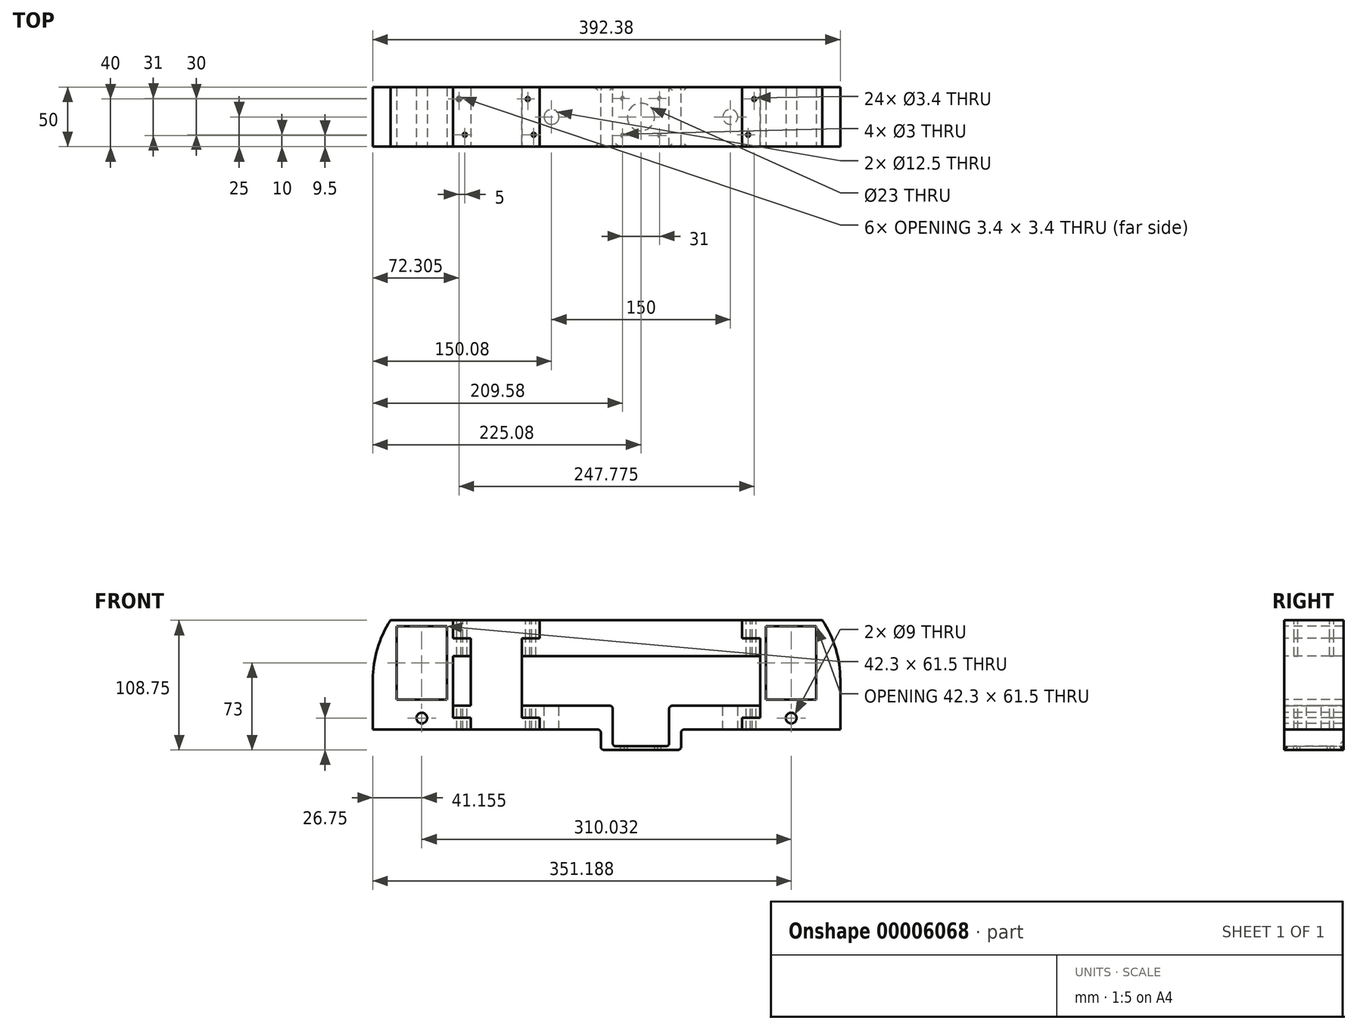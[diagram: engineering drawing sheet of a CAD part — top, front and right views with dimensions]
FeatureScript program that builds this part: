
annotation { "Feature Type Name" : "Feature", "Feature Type Description" : "" }
export const myFeature = defineFeature(function(context is Context, id is Id, definition is map)
    precondition{}
    {
        {
            var Q0;
            Q0=qCreatedBy(makeId("Front.planeOp"),FACE);
            var sketch = newSketch(context, id + "F0", { "sketchPlane" : qUnion([Q0])});
            skLineSegment(sketch, "E0", {"start": v(66.35, 0) * mm, "end": v(66.35, -17) * mm});
            skLineSegment(sketch, "E1", {"start": v(66.35, -17) * mm, "end": v(133.65, -17) * mm});
            skLineSegment(sketch, "E2", {"start": v(133.65, -17) * mm, "end": v(133.65, 0) * mm});
            skLineSegment(sketch, "E3", {"start": v(200, 20) * mm, "end": v(123.65, 20) * mm});
            skLineSegment(sketch, "E4", {"start": v(123.65, 20) * mm, "end": v(123.65, -14) * mm});
            skLineSegment(sketch, "E5", {"start": v(123.65, -14) * mm, "end": v(76.35, -14) * mm});
            skLineSegment(sketch, "E6", {"start": v(76.35, -14) * mm, "end": v(76.35, 20) * mm});
            skLineSegment(sketch, "E7", {"start": v(76.35, 20) * mm, "end": v(0, 20) * mm});
            skLineSegment(sketch, "E8", {"start": v(133.65, 0) * mm, "end": v(185, 0) * mm});
            skLineSegment(sketch, "E9", {"start": v(185, 0) * mm, "end": v(185, 10) * mm});
            skLineSegment(sketch, "E10", {"start": v(185, 10) * mm, "end": v(200, 10) * mm});
            skLineSegment(sketch, "E11", {"start": v(200, 10) * mm, "end": v(200, 20) * mm});
            skLineSegment(sketch, "E12", {"start": v(66.35, 0) * mm, "end": v(15, 0) * mm});
            skLineSegment(sketch, "E13", {"start": v(15, 0) * mm, "end": v(15, 10) * mm});
            skLineSegment(sketch, "E14", {"start": v(15, 10) * mm, "end": v(0, 10) * mm});
            skLineSegment(sketch, "E15", {"start": v(0, 10) * mm, "end": v(0, 20) * mm});
            skSolve(sketch);
        }
        {
            var Q0;
            Q0 = qSketchRegion(id + "F0", true);
            extrude(context, id + "F1", {"entities" : qUnion([Q0]), "depth" : 50 * mm});
        }
        {
            var Q0;
            Q0=makeQuery(id+"F1.opExtrude","SWEPT_EDGE",EDGE,{"disambiguationData":[OSD([sQuery(id+"F0.wireOp",EDGE,"E4"),sQuery(id+"F0.wireOp",EDGE,"E5")])]});
            var Q1;
            Q1=makeQuery(id+"F1.opExtrude","SWEPT_EDGE",EDGE,{"disambiguationData":[OSD([sQuery(id+"F0.wireOp",EDGE,"E5"),sQuery(id+"F0.wireOp",EDGE,"E6")])]});
            var Q2;
            Q2=makeQuery(id+"F1.opExtrude","SWEPT_EDGE",EDGE,{"disambiguationData":[OSD([sQuery(id+"F0.wireOp",EDGE,"E1"),sQuery(id+"F0.wireOp",EDGE,"E2")])]});
            var Q3;
            Q3=makeQuery(id+"F1.opExtrude","SWEPT_EDGE",EDGE,{"disambiguationData":[OSD([sQuery(id+"F0.wireOp",EDGE,"E0"),sQuery(id+"F0.wireOp",EDGE,"E1")])]});
            var Q4;
            Q4=makeQuery(id+"F1.opExtrude","SWEPT_EDGE",EDGE,{"disambiguationData":[OSD([sQuery(id+"F0.wireOp",EDGE,"25d413c4-04d7-459c-bcf7-bf226ccfaa6d"),sQuery(id+"F0.wireOp",EDGE,"E0")])]});
            var Q5;
            Q5=makeQuery(id+"F1.opExtrude","SWEPT_EDGE",EDGE,{"disambiguationData":[OSD([sQuery(id+"F0.wireOp",EDGE,"E2"),sQuery(id+"F0.wireOp",EDGE,"8273c938-ca82-47b6-a2fe-12fa87529be1")])]});
            var Q6;
            Q6=makeQuery(id+"F1.opExtrude","SWEPT_EDGE",EDGE,{"disambiguationData":[OSD([sQuery(id+"F0.wireOp",EDGE,"E3"),sQuery(id+"F0.wireOp",EDGE,"E4")])]});
            var Q7;
            Q7=makeQuery(id+"F1.opExtrude","SWEPT_EDGE",EDGE,{"disambiguationData":[OSD([sQuery(id+"F0.wireOp",EDGE,"E6"),sQuery(id+"F0.wireOp",EDGE,"E7")])]});
            var Q8;
            Q8=makeQuery(id+"F1.opExtrude","CAP_EDGE",EDGE,{"disambiguationData":[OSD([sQuery(id+"F0.wireOp",EDGE,"E7")])],"isStart":false});
            var Q9;
            Q9=makeQuery(id+"F1.opExtrude","CAP_EDGE",EDGE,{"disambiguationData":[OSD([sQuery(id+"F0.wireOp",EDGE,"E3")])],"isStart":false});
            var Q10;
            Q10=makeQuery(id+"F1.opExtrude","CAP_EDGE",EDGE,{"disambiguationData":[OSD([sQuery(id+"F0.wireOp",EDGE,"E3")])],"isStart":true});
            var Q11;
            Q11=makeQuery(id+"F1.opExtrude","CAP_EDGE",EDGE,{"disambiguationData":[OSD([sQuery(id+"F0.wireOp",EDGE,"E7")])],"isStart":true});
            var Q12;
            Q12=makeQuery(id+"F1.opExtrude","CAP_EDGE",EDGE,{"disambiguationData":[OSD([sQuery(id+"F0.wireOp",EDGE,"E6")])],"isStart":false});
            var Q13;
            Q13=makeQuery(id+"F1.opExtrude","CAP_EDGE",EDGE,{"disambiguationData":[OSD([sQuery(id+"F0.wireOp",EDGE,"E2")])],"isStart":false});
            var Q14;
            Q14=makeQuery(id+"F1.opExtrude","CAP_EDGE",EDGE,{"disambiguationData":[OSD([sQuery(id+"F0.wireOp",EDGE,"E0")])],"isStart":false});
            var Q15;
            Q15=makeQuery(id+"F1.opExtrude","CAP_EDGE",EDGE,{"disambiguationData":[OSD([sQuery(id+"F0.wireOp",EDGE,"E5")])],"isStart":true});
            var Q16;
            Q16=makeQuery(id+"F1.opExtrude","CAP_EDGE",EDGE,{"disambiguationData":[OSD([sQuery(id+"F0.wireOp",EDGE,"E2")])],"isStart":true});
            var Q17;
            Q17=makeQuery(id+"F1.opExtrude","CAP_EDGE",EDGE,{"disambiguationData":[OSD([sQuery(id+"F0.wireOp",EDGE,"E0")])],"isStart":true});
            fillet(context, id + "F2", {"entities" : qUnion([Q0, Q1, Q2, Q3, Q4, Q5, Q6, Q7, Q8, Q9, Q10, Q11, Q12, Q13, Q14, Q15, Q16, Q17]), "radius" : 2.5 * mm, "tangentPropagation" : true, "allowEdgeOverflow" : false});
        }
        {
            var Q0;
            Q0=makeQuery(id+"F1.opExtrude","SWEPT_FACE",FACE,{"disambiguationData":[OSD([sQuery(id+"F0.wireOp",EDGE,"E5")])]});
            var sketch = newSketch(context, id + "F3", { "sketchPlane" : qUnion([Q0])});
            skLineSegment(sketch, "E16.bottom", {"start": v(78.85, -3.85) * mm, "end": v(121.15, -3.85) * mm, "construction": true});
            skLineSegment(sketch, "E16.top", {"start": v(78.85, -46.15) * mm, "end": v(121.15, -46.15) * mm, "construction": true});
            skLineSegment(sketch, "E16.left", {"start": v(78.85, -3.85) * mm, "end": v(78.85, -46.15) * mm, "construction": true});
            skLineSegment(sketch, "E16.right", {"start": v(121.15, -3.85) * mm, "end": v(121.15, -46.15) * mm, "construction": true});
            skLineSegment(sketch, "E17", {"start": v(100, -3.85) * mm, "end": v(100, -2.5) * mm, "construction": true});
            skLineSegment(sketch, "E18", {"start": v(100, -46.15) * mm, "end": v(100, -47.5) * mm, "construction": true});
            skLineSegment(sketch, "E19", {"start": v(78.85, -3.85) * mm, "end": v(121.15, -46.15) * mm, "construction": true});
            skLineSegment(sketch, "E20", {"start": v(78.85, -46.15) * mm, "end": v(121.15, -3.85) * mm, "construction": true});
            skLineSegment(sketch, "E21", {"start": v(84.5, -9.5) * mm, "end": v(115.5, -9.5) * mm, "construction": true});
            skLineSegment(sketch, "E22", {"start": v(115.5, -9.5) * mm, "end": v(115.5, -40.5) * mm, "construction": true});
            skLineSegment(sketch, "E23", {"start": v(115.5, -40.5) * mm, "end": v(84.5, -40.5) * mm, "construction": true});
            skLineSegment(sketch, "E24", {"start": v(84.5, -40.5) * mm, "end": v(84.5, -9.5) * mm, "construction": true});
            skCircle(sketch, "E25", {"center": v(84.5, -9.5) * mm, "radius": 1.5 * mm});
            skCircle(sketch, "E26", {"center": v(115.5, -9.5) * mm, "radius": 1.5 * mm});
            skCircle(sketch, "E27", {"center": v(115.5, -40.5) * mm, "radius": 1.5 * mm});
            skCircle(sketch, "E28", {"center": v(84.5, -40.5) * mm, "radius": 1.5 * mm});
            skCircle(sketch, "E29", {"center": v(100, -25) * mm, "radius": 11.5 * mm});
            skSolve(sketch);
        }
        {
            var Q0;
            Q0 = qSketchRegion(id + "F3", true);
            extrude(context, id + "F4", {"entities" : qUnion([Q0]), "operationType" : NewBodyOperationType.REMOVE, "oppositeDirection" : true, "depth" : 25 * mm});
        }
        {
            var Q0;
            Q0=makeQuery(id+"F1.opExtrude","CAP_FACE",FACE,{"disambiguationData":[OSD([sQuery(id+"F0.wireOp",EDGE,"7cd8d7bc-7dec-443a-83b3-ba99ea593d57"),sQuery(id+"F0.wireOp",EDGE,"59747b56-2e24-4794-8826-f2c9fe0a8e2f"),sQuery(id+"F0.wireOp",EDGE,"60e4274c-6528-4dbb-8c65-7a1c295b8255"),sQuery(id+"F0.wireOp",EDGE,"69b43952-8336-45bf-9730-06b1f1448a6f"),sQuery(id+"F0.wireOp",EDGE,"a2af3474-0233-43bb-83cb-60ed80dac262"),sQuery(id+"F0.wireOp",EDGE,"25d413c4-04d7-459c-bcf7-bf226ccfaa6d"),sQuery(id+"F0.wireOp",EDGE,"E0"),sQuery(id+"F0.wireOp",EDGE,"E1"),sQuery(id+"F0.wireOp",EDGE,"E2"),sQuery(id+"F0.wireOp",EDGE,"8273c938-ca82-47b6-a2fe-12fa87529be1"),sQuery(id+"F0.wireOp",EDGE,"4707e04e-d9cc-4bb7-a771-f1b94968c0b5"),sQuery(id+"F0.wireOp",EDGE,"26d6e5ed-fd12-44b5-9e14-1d22e9212bdb"),sQuery(id+"F0.wireOp",EDGE,"6fa0b8f3-1a7a-4232-9b85-c42c3082a16d"),sQuery(id+"F0.wireOp",EDGE,"91bd62d1-c68c-4093-848f-cc9b293d17f5"),sQuery(id+"F0.wireOp",EDGE,"8c203d04-b222-4ccc-a70f-71613ceaa2ef"),sQuery(id+"F0.wireOp",EDGE,"E3"),sQuery(id+"F0.wireOp",EDGE,"E4"),sQuery(id+"F0.wireOp",EDGE,"E5"),sQuery(id+"F0.wireOp",EDGE,"E6"),sQuery(id+"F0.wireOp",EDGE,"E7")])],"isStart":false});
            var sketch = newSketch(context, id + "F5", { "sketchPlane" : qUnion([Q0])});
            skLineSegment(sketch, "E30", {"start": v(247.26, 86.75) * mm, "end": v(204.96, 86.75) * mm});
            skLineSegment(sketch, "E31", {"start": v(226.1, 86.75) * mm, "end": v(226.1, -5.25) * mm, "construction": true});
            skCircle(sketch, "E32", {"center": v(226.1, 9.75) * mm, "radius": 4.5 * mm});
            skLineSegment(sketch, "E33", {"start": v(226.1, 9.75) * mm, "end": v(226.1, 25.25) * mm, "construction": true});
            skLineSegment(sketch, "E34", {"start": v(226.1, 25.25) * mm, "end": v(204.96, 25.25) * mm});
            skLineSegment(sketch, "E35", {"start": v(204.96, 25.25) * mm, "end": v(204.96, 86.75) * mm});
            skLineSegment(sketch, "E36.bottom", {"start": v(267.3, 91.75) * mm, "end": v(252.3, 91.75) * mm, "construction": true});
            skLineSegment(sketch, "E36.top", {"start": v(267.3, 41.75) * mm, "end": v(252.3, 41.75) * mm, "construction": true});
            skLineSegment(sketch, "E36.left", {"start": v(267.3, 91.75) * mm, "end": v(267.3, 41.75) * mm, "construction": true});
            skLineSegment(sketch, "E36.right", {"start": v(252.3, 91.75) * mm, "end": v(252.3, 41.75) * mm, "construction": true});
            skLineSegment(sketch, "E37", {"start": v(252.3, 91.75) * mm, "end": v(200, 91.75) * mm});
            skArc(sketch, "E38", {"start": v(267.3, 41.75) * mm, "mid": v(263.47, 67.85) * mm, "end": v(252.3, 91.75) * mm});
            skLineSegment(sketch, "E39", {"start": v(226.1, 25.25) * mm, "end": v(247.26, 25.25) * mm});
            skLineSegment(sketch, "E40", {"start": v(247.26, 86.75) * mm, "end": v(247.26, 25.25) * mm});
            skLineSegment(sketch, "E41", {"start": v(185, 10) * mm, "end": v(200, 10) * mm});
            skLineSegment(sketch, "E42", {"start": v(200, 91.75) * mm, "end": v(185, 91.75) * mm});
            skLineSegment(sketch, "E43", {"start": v(185, 91.75) * mm, "end": v(185, 76.75) * mm});
            skLineSegment(sketch, "E44", {"start": v(185, 76.75) * mm, "end": v(200, 76.75) * mm});
            skLineSegment(sketch, "E45", {"start": v(200, 10) * mm, "end": v(200, 76.75) * mm});
            skLineSegment(sketch, "E46", {"start": v(185, 10) * mm, "end": v(185, 0) * mm});
            skLineSegment(sketch, "E47", {"start": v(185, 0) * mm, "end": v(267.3, 0) * mm});
            skLineSegment(sketch, "E48", {"start": v(267.3, 41.75) * mm, "end": v(267.3, 0) * mm});
            skSolve(sketch);
        }
        {
            var Q0;
            Q0=makeQuery(id+"F1.opExtrude","SWEPT_FACE",FACE,{"disambiguationData":[OSD([sQuery(id+"F0.wireOp",EDGE,"E7")])]});
            var sketch = newSketch(context, id + "F6", { "sketchPlane" : qUnion([Q0])});
            skCircle(sketch, "E49", {"center": v(25, -25) * mm, "radius": 6.25 * mm});
            skCircle(sketch, "E50", {"center": v(175, -25) * mm, "radius": 6.25 * mm});
            skCircle(sketch, "E51", {"center": v(5, -10) * mm, "radius": 1.7 * mm});
            skCircle(sketch, "E52", {"center": v(10, -40) * mm, "radius": 1.7 * mm});
            skCircle(sketch, "E53", {"center": v(190, -40) * mm, "radius": 1.7 * mm});
            skCircle(sketch, "E54", {"center": v(195, -10) * mm, "radius": 1.7 * mm});
            skSolve(sketch);
        }
        {
            var Q0;
            Q0 = qSketchRegion(id + "F6", true);
            extrude(context, id + "F7", {"entities" : qUnion([Q0]), "operationType" : NewBodyOperationType.REMOVE, "endBound" : BoundingType.THROUGH_ALL, "depth" : 25 * mm});
        }
        {
            var Q0;
            Q0 = qSketchRegion(id + "F5", true);
            extrude(context, id + "F8", {"entities" : qUnion([Q0]), "oppositeDirection" : true, "depth" : 50 * mm});
        }
        {
            var Q0;
            Q0=makeQuery(id+"F8.opExtrude","CAP_FACE",FACE,{"disambiguationData":[OSD([sQuery(id+"F5.wireOp",EDGE,"E30"),sQuery(id+"F5.wireOp",EDGE,"E32"),sQuery(id+"F5.wireOp",EDGE,"E34"),sQuery(id+"F5.wireOp",EDGE,"E35"),sQuery(id+"F5.wireOp",EDGE,"E37"),sQuery(id+"F5.wireOp",EDGE,"E38"),sQuery(id+"F5.wireOp",EDGE,"E39"),sQuery(id+"F5.wireOp",EDGE,"E40"),sQuery(id+"F5.wireOp",EDGE,"E41"),sQuery(id+"F5.wireOp",EDGE,"E42"),sQuery(id+"F5.wireOp",EDGE,"E43"),sQuery(id+"F5.wireOp",EDGE,"E44"),sQuery(id+"F5.wireOp",EDGE,"E45"),sQuery(id+"F5.wireOp",EDGE,"E46"),sQuery(id+"F5.wireOp",EDGE,"E47"),sQuery(id+"F5.wireOp",EDGE,"E48")])],"isStart":true});
            var sketch = newSketch(context, id + "F9", { "sketchPlane" : qUnion([Q0])});
            skLineSegment(sketch, "E55", {"start": v(200, 76.75) * mm, "end": v(200, 61.75) * mm});
            skLineSegment(sketch, "E56", {"start": v(200, 76.75) * mm, "end": v(185, 76.75) * mm});
            skLineSegment(sketch, "E57", {"start": v(185, 76.75) * mm, "end": v(185, 91.75) * mm});
            skLineSegment(sketch, "E58", {"start": v(185, 91.75) * mm, "end": v(15, 91.75) * mm});
            skLineSegment(sketch, "E59", {"start": v(15, 91.75) * mm, "end": v(15, 76.75) * mm});
            skLineSegment(sketch, "E60", {"start": v(15, 76.75) * mm, "end": v(0, 76.75) * mm});
            skLineSegment(sketch, "E61", {"start": v(0, 76.75) * mm, "end": v(0, 61.75) * mm});
            skLineSegment(sketch, "E62", {"start": v(0, 61.75) * mm, "end": v(200, 61.75) * mm});
            skSolve(sketch);
        }
        {
            var Q0;
            Q0 = qSketchRegion(id + "F9", true);
            extrude(context, id + "F10", {"entities" : qUnion([Q0]), "oppositeDirection" : true, "depth" : 50 * mm});
        }
        {
            var Q0;
            Q0=makeQuery(id+"F10.opExtrude","CAP_FACE",FACE,{"disambiguationData":[OSD([sQuery(id+"F9.wireOp",EDGE,"E55"),sQuery(id+"F9.wireOp",EDGE,"E56"),sQuery(id+"F9.wireOp",EDGE,"E57"),sQuery(id+"F9.wireOp",EDGE,"E58"),sQuery(id+"F9.wireOp",EDGE,"E59"),sQuery(id+"F9.wireOp",EDGE,"E60"),sQuery(id+"F9.wireOp",EDGE,"E61"),sQuery(id+"F9.wireOp",EDGE,"E62")])],"isStart":true});
            var sketch = newSketch(context, id + "F11", { "sketchPlane" : qUnion([Q0])});
            skLineSegment(sketch, "E63", {"start": v(15, 91.75) * mm, "end": v(15, 76.75) * mm});
            skLineSegment(sketch, "E64", {"start": v(15, 76.75) * mm, "end": v(0, 76.75) * mm});
            skLineSegment(sketch, "E65", {"start": v(0, 76.75) * mm, "end": v(0, 10) * mm});
            skLineSegment(sketch, "E66", {"start": v(0, 10) * mm, "end": v(15, 10) * mm});
            skLineSegment(sketch, "E67", {"start": v(15, 10) * mm, "end": v(15, 0) * mm});
            skLineSegment(sketch, "E68", {"start": v(15, 0) * mm, "end": v(-42.78, 0) * mm});
            skLineSegment(sketch, "E69", {"start": v(-42.78, 0) * mm, "end": v(-42.78, 10) * mm});
            skLineSegment(sketch, "E70", {"start": v(-42.78, 10) * mm, "end": v(-57.78, 10) * mm});
            skLineSegment(sketch, "E71", {"start": v(-57.78, 10) * mm, "end": v(-57.78, 20) * mm});
            skLineSegment(sketch, "E72", {"start": v(-57.78, 20) * mm, "end": v(-42.78, 20) * mm});
            skLineSegment(sketch, "E73", {"start": v(-42.78, 20) * mm, "end": v(-42.78, 76.75) * mm});
            skLineSegment(sketch, "E74", {"start": v(-42.78, 76.75) * mm, "end": v(-57.78, 76.75) * mm});
            skLineSegment(sketch, "E75", {"start": v(-57.78, 76.75) * mm, "end": v(-57.78, 91.75) * mm});
            skLineSegment(sketch, "E76", {"start": v(-57.78, 91.75) * mm, "end": v(15, 91.75) * mm});
            skSolve(sketch);
        }
        {
            var Q0;
            Q0 = qSketchRegion(id + "F11", true);
            extrude(context, id + "F12", {"entities" : qUnion([Q0]), "oppositeDirection" : true, "depth" : 50 * mm});
        }
        {
            var Q0;
            Q0=makeQuery(id+"F12.opExtrude","CAP_FACE",FACE,{"disambiguationData":[OSD([sQuery(id+"F11.wireOp",EDGE,"E63"),sQuery(id+"F11.wireOp",EDGE,"E64"),sQuery(id+"F11.wireOp",EDGE,"E65"),sQuery(id+"F11.wireOp",EDGE,"E66"),sQuery(id+"F11.wireOp",EDGE,"E67"),sQuery(id+"F11.wireOp",EDGE,"E68"),sQuery(id+"F11.wireOp",EDGE,"E69"),sQuery(id+"F11.wireOp",EDGE,"E70"),sQuery(id+"F11.wireOp",EDGE,"E71"),sQuery(id+"F11.wireOp",EDGE,"E72"),sQuery(id+"F11.wireOp",EDGE,"E73"),sQuery(id+"F11.wireOp",EDGE,"E74"),sQuery(id+"F11.wireOp",EDGE,"E75"),sQuery(id+"F11.wireOp",EDGE,"E76"),sQuery(id+"F11.wireOp",EDGE,"a7328c5a-23c9-4590-84e1-86b060998002"),sQuery(id+"F11.wireOp",EDGE,"49678679-c78d-463e-80d5-f9fdda81f58f"),sQuery(id+"F11.wireOp",EDGE,"c6644c5c-7cd0-4a62-a678-3d565e289008"),sQuery(id+"F11.wireOp",EDGE,"f0cade5a-4763-4761-80b8-ea56b3358b8d")])],"isStart":true});
            var sketch = newSketch(context, id + "F13", { "sketchPlane" : qUnion([Q0])});
            skLineSegment(sketch, "E77", {"start": v(-42.78, 76.75) * mm, "end": v(-57.78, 76.75) * mm});
            skLineSegment(sketch, "E78", {"start": v(-57.78, 76.75) * mm, "end": v(-57.78, 91.75) * mm});
            skLineSegment(sketch, "E79", {"start": v(-110.08, 91.75) * mm, "end": v(-125.08, 91.75) * mm, "construction": true});
            skLineSegment(sketch, "E80", {"start": v(-125.08, 91.75) * mm, "end": v(-125.08, 41.75) * mm, "construction": true});
            skLineSegment(sketch, "E81", {"start": v(-125.08, 41.75) * mm, "end": v(-110.08, 41.75) * mm, "construction": true});
            skLineSegment(sketch, "E82", {"start": v(-110.08, 41.75) * mm, "end": v(-110.08, 91.75) * mm, "construction": true});
            skArc(sketch, "E83", {"start": v(-110.08, 91.75) * mm, "mid": v(-121.24, 67.85) * mm, "end": v(-125.08, 41.75) * mm});
            skLineSegment(sketch, "E84", {"start": v(-125.08, 41.75) * mm, "end": v(-125.08, 0) * mm});
            skLineSegment(sketch, "E85", {"start": v(-125.08, 0) * mm, "end": v(-42.78, 0) * mm});
            skLineSegment(sketch, "E86", {"start": v(-42.78, 0) * mm, "end": v(-42.78, 10) * mm});
            skLineSegment(sketch, "E87", {"start": v(-42.78, 10) * mm, "end": v(-57.78, 10) * mm});
            skLineSegment(sketch, "E88", {"start": v(-57.78, 10) * mm, "end": v(-57.78, 20) * mm});
            skLineSegment(sketch, "E89", {"start": v(-42.78, 76.75) * mm, "end": v(-42.78, 61.75) * mm});
            skLineSegment(sketch, "E90", {"start": v(-42.78, 61.75) * mm, "end": v(-57.78, 61.75) * mm});
            skLineSegment(sketch, "E91", {"start": v(-57.78, 61.75) * mm, "end": v(-57.78, 20) * mm});
            skLineSegment(sketch, "E92", {"start": v(-110.08, 91.75) * mm, "end": v(-57.78, 91.75) * mm});
            skLineSegment(sketch, "E93", {"start": v(-62.78, 91.75) * mm, "end": v(-62.78, 86.75) * mm, "construction": true});
            skLineSegment(sketch, "E94", {"start": v(-62.78, 86.75) * mm, "end": v(-57.78, 86.75) * mm, "construction": true});
            skLineSegment(sketch, "E95", {"start": v(-62.78, 86.75) * mm, "end": v(-105.08, 86.75) * mm});
            skLineSegment(sketch, "E96", {"start": v(-105.08, 86.75) * mm, "end": v(-105.08, 25.25) * mm});
            skLineSegment(sketch, "E97", {"start": v(-105.08, 25.25) * mm, "end": v(-62.78, 25.25) * mm});
            skLineSegment(sketch, "E98", {"start": v(-62.78, 25.25) * mm, "end": v(-62.78, 86.75) * mm});
            skLineSegment(sketch, "E99", {"start": v(-83.93, 86.75) * mm, "end": v(-83.93, 0) * mm, "construction": true});
            skPoint(sketch, "E100", {"position": v(-83.93, 25.25) * mm});
            skCircle(sketch, "E101", {"center": v(-83.93, 9.75) * mm, "radius": 4.5 * mm});
            skSolve(sketch);
        }
        {
            var Q0;
            Q0 = qSketchRegion(id + "F13", true);
            extrude(context, id + "F14", {"entities" : qUnion([Q0]), "oppositeDirection" : true, "depth" : 50 * mm});
        }
        {
            var Q0;
            Q0 = qSketchRegion(id + "F6", true);
            extrude(context, id + "F15", {"entities" : qUnion([Q0]), "operationType" : NewBodyOperationType.REMOVE, "endBound" : BoundingType.THROUGH_ALL, "oppositeDirection" : true, "depth" : 25 * mm});
        }
        {
            var Q0;
            Q0=makeQuery(id+"F12.opExtrude","SWEPT_FACE",FACE,{"disambiguationData":[OSD([sQuery(id+"F11.wireOp",EDGE,"E76")])]});
            var sketch = newSketch(context, id + "F16", { "sketchPlane" : qUnion([Q0])});
            skLineSegment(sketch, "E102.bottom", {"start": v(-57.78, -50) * mm, "end": v(-42.78, -50) * mm, "construction": true});
            skLineSegment(sketch, "E102.top", {"start": v(-57.78, 0) * mm, "end": v(-42.78, 0) * mm, "construction": true});
            skLineSegment(sketch, "E102.left", {"start": v(-57.78, -50) * mm, "end": v(-57.78, 0) * mm, "construction": true});
            skLineSegment(sketch, "E102.right", {"start": v(-42.78, -50) * mm, "end": v(-42.78, 0) * mm, "construction": true});
            skLineSegment(sketch, "E103", {"start": v(-47.78, 0) * mm, "end": v(-47.78, -50) * mm, "construction": true});
            skLineSegment(sketch, "E104", {"start": v(-52.78, 0) * mm, "end": v(-52.78, -50) * mm, "construction": true});
            skLineSegment(sketch, "E105", {"start": v(-57.78, -40) * mm, "end": v(-42.78, -40) * mm, "construction": true});
            skLineSegment(sketch, "E106", {"start": v(-57.78, -10) * mm, "end": v(-42.78, -10) * mm, "construction": true});
            skCircle(sketch, "E107", {"center": v(-47.78, -40) * mm, "radius": 1.7 * mm});
            skCircle(sketch, "E108", {"center": v(-52.78, -10) * mm, "radius": 1.7 * mm});
            skSolve(sketch);
        }
        {
            var Q0;
            Q0 = qSketchRegion(id + "F16", true);
            var Q1;
            Q1=makeQuery(id+"F14.opExtrude","SWEPT_FACE",FACE,{"disambiguationData":[OSD([sQuery(id+"F13.wireOp",EDGE,"E85")])]});
            extrude(context, id + "F17", {"entities" : qUnion([Q0]), "operationType" : NewBodyOperationType.REMOVE, "endBound" : BoundingType.THROUGH_ALL, "oppositeDirection" : true, "endBoundEntity" : qUnion([Q1]), "depth" : 92.5 * mm});
        }
        {
            var Q0;
            Q0=makeQuery(id+"F10.opExtrude","SWEPT_FACE",FACE,{"disambiguationData":[OSD([sQuery(id+"F9.wireOp",EDGE,"E58")])]});
            var sketch = newSketch(context, id + "F18", { "sketchPlane" : qUnion([Q0])});
            skCircle(sketch, "E109", {"center": v(5, -10) * mm, "radius": 1.7 * mm});
            skCircle(sketch, "E110", {"center": v(10, -40) * mm, "radius": 1.7 * mm});
            skCircle(sketch, "E111", {"center": v(195, -10) * mm, "radius": 1.7 * mm});
            skCircle(sketch, "E112", {"center": v(190, -40) * mm, "radius": 1.7 * mm});
            skSolve(sketch);
        }
        {
            var Q0;
            Q0 = qSketchRegion(id + "F18", true);
            extrude(context, id + "F19", {"entities" : qUnion([Q0]), "operationType" : NewBodyOperationType.REMOVE, "oppositeDirection" : true, "depth" : 30 * mm});
        }
    });
